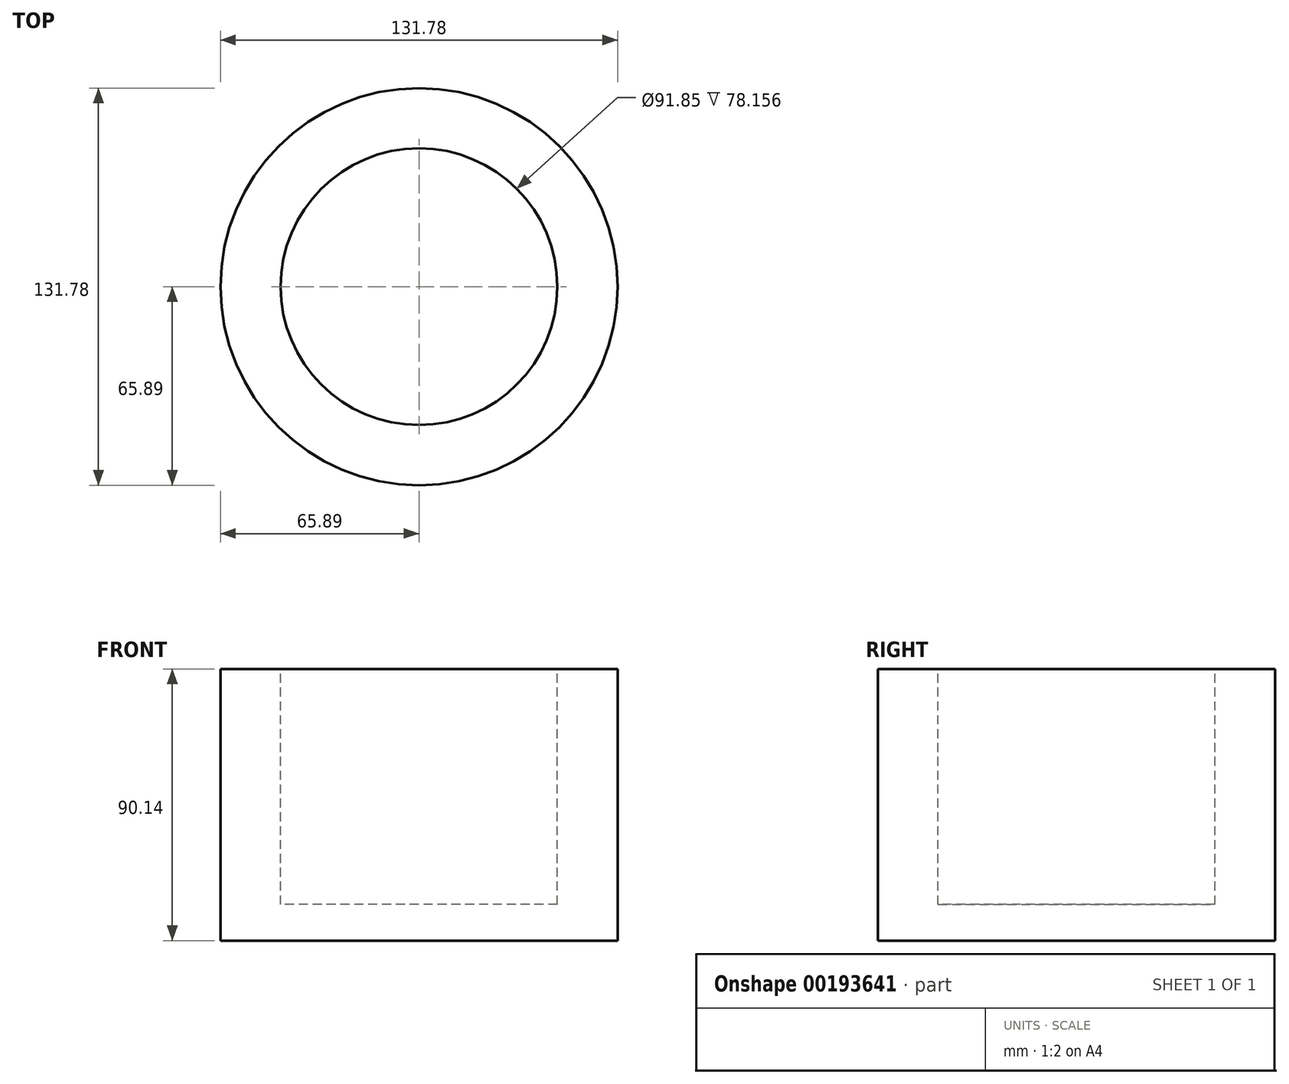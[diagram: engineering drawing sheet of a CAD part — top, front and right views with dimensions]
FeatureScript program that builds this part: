
annotation { "Feature Type Name" : "Feature", "Feature Type Description" : "" }
export const myFeature = defineFeature(function(context is Context, id is Id, definition is map)
    precondition{}
    {
        {
            var Q0;
            Q0=qCreatedBy(makeId("Front.planeOp"),FACE);
            var sketch = newSketch(context, id + "F0", { "sketchPlane" : qUnion([Q0])});
            skLineSegment(sketch, "E0", {"start": v(0, 0) * mm, "end": v(0, 45.5) * mm});
            skLineSegment(sketch, "E1", {"start": v(0, 45.5) * mm, "end": v(0, -41.79) * mm});
            skLineSegment(sketch, "E2", {"start": v(0, -41.79) * mm, "end": v(65.9, -41.79) * mm});
            skLineSegment(sketch, "E3", {"start": v(65.9, -41.79) * mm, "end": v(65.9, 48.35) * mm});
            skLineSegment(sketch, "E4", {"start": v(65.9, 48.35) * mm, "end": v(45.92, 48.35) * mm});
            skLineSegment(sketch, "E5", {"start": v(45.92, 48.35) * mm, "end": v(45.92, -29.8) * mm});
            skLineSegment(sketch, "E6", {"start": v(45.92, -29.8) * mm, "end": v(0, -29.8) * mm});
            skSolve(sketch);
        }
        {
            var Q0;
            {var subQ0=sQuery(id+"F0.wireOp",EDGE,"E2");Q0=makeQuery(id+"F0.imprint","IMPRINT",FACE,{"disambiguationData":[TD([[makeQuery(id+"F0.imprint","IMPRINT",EDGE,{"derivedFrom":subQ0}),1.0]])]});}
            var Q1;
            Q1=sQuery(id+"F0.wireOp",EDGE,"E1");
            revolve(context, id + "F1", {"entities" : qUnion([Q0]), "axis" : qUnion([Q1]), "revolveType" : RevolveType.FULL});
        }
    });
